# Revit family: 403203 WALLBOX MINI ASYMMETRIC 01
name_source: partatom
category: Apparecchi per illuminazione
units: mm (PartAtom-declared; Revit-internal decimal feet)

## family parameters
Basato su piano di lavoro = No
Condiviso = Sì
Mantieni orientamento annotazione = No
Punto di calcolo locali = No
Quota connettore circolare = Usa diametro
Sempre verticale = Sì
Sorgente d'illuminazione = Sì
Taglio con vuoti quando caricato = No
Tipo di parte = Normale

## types (1)
- ALLOY
    Angolo inclinazione = 0.00°
    Available Optics = ASYMMETRICAL WIDE LIGHT ONE SIDE DISTRIBUTION
    Colori = 2.700°K on request
    Commenti sul wattaggio = CLASS  I
    Filtro dei colori = 16777215
    Finish color = Alloy Antracite RAL7016
    IP Rating = IP66
    Ligjt Source = LED
    Material = extruded copper-free aluminum
    Modello = WALLBOX MINI ASYMMETRIC 01
    Produttore = PUK
    Prospetto di default = 2023 mm
    Variazione temperatura colore lampada con luminosità attenuata = <Nessuno>
    Voltage = 220-240V  50-60Hz
    Wattage = 8W
